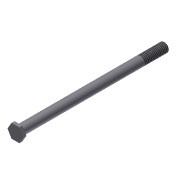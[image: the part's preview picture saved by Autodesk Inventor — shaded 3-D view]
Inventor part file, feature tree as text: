
AUTODESK INVENTOR PART (.ipt)
format: ipt  version: 2011 (Build 150239000, 239)  size: 86,528 bytes
history: native  units: in
note: dims shown in document units (in); Inventor stores cm internally (conversion verified against a paired STEP export)
features: extrude x2, sketch x2, thread x1, chamfer x1
ambient origin geometry x8: Origin, YZ Plane, XZ Plane, XY Plane, X Axis, Y Axis, Z Axis, Center Point
bodies: Solid1 (feature_tree)
feature tree (6):
  extrude  "Extrusion1"  Depth=6.0in TaperAngle=0.0deg
  extrude  "Extrusion2"  Depth=0.125in TaperAngle=0.0deg
  thread  "Thread1"  [1 undecoded]
  chamfer  "Chamfer1"  Distance=0.02in Angle=45.0deg
  sketch  "Sketch1"  dims[d0=0.375in d1=6.0in d2=0.0in]
  sketch  "Sketch2"  dims[d3=0.5625in d4=0.125in d5=0.0in d6=1.0in d7=0.0in d8=0.02in d9=0.125in d10=45.0deg]
note: 1 required parameter value undecoded (feature->parameter linkage not recoverable at this tier; creation-order binding heuristic only, values carry confidence <= 0.55)
